FCSTD DOCUMENT  (FreeCAD 0.20R29603 (Git))
Label: cockpit
License: All rights reserved
LicenseURL: http://en.wikipedia.org/wiki/All_rights_reserved
objects: Part::FeaturePython×22, Part::Cylinder×14, Part::Cut×11, Part::MultiFuse×9, Part::Fillet×8, Part::Box×6, Sketcher::SketchObject×4, PartDesign::Pad×4, PartDesign::Body×4, Part::Chamfer×4, Part::Feature×3, Part::Refine×2, Part::Prism×2, Mesh::Feature×1, App::DocumentObjectGroup×1
note: 97 computed .brp shape members not serialized (recipe doc carries the construction recipe); baked Part::Feature solids carry a one-line shape summary decoded from their .brp

FEATURE [Part::Feature] Part__Feature  label="Motedis_45x45"
  Placement = pos=(3,45,0) rot=(0,0,1;0rad)
  shape: bbox 45 x 45 x 1000 mm, 210 faces (baked)
FEATURE [Part::Feature] Part__Feature001  label="Motedis_45x90"
  Placement = pos=(36.25,1.5,0) rot=(0,0,1;0rad)
  shape: bbox 90 x 45 x 1000 mm, 334 faces (baked)
FEATURE [Part::Refine] Part__Feature002  label="Motedis_45x45_refined"
  Source = -> Part__Feature
FEATURE [Part::Refine] Part__Feature001001  label="Motedis_45x90_refined"
  Source = -> Part__Feature001
FEATURE [Part::FeaturePython] Clone  label="Motedis_45x90_refined001"  # Draft clone (typed FeaturePython)
  AttacherType = Attacher::AttachEngine3D
  Fuse = false
  Objects = -> [Part__Feature001001]
  Placement = pos=(0,545,90) rot=(0,1,0;1.5708rad)
  Scale = (1,1,1.3)
FEATURE [Part::FeaturePython] Clone001  label="Motedis_45x90_refined002"  # Draft clone (typed FeaturePython)
  AttacherType = Attacher::AttachEngine3D
  Fuse = false
  Objects = -> [Part__Feature001001]
  Placement = pos=(0,0,90) rot=(0,1,0;1.5708rad)
  Scale = (1,1,1.3)
FEATURE [Part::FeaturePython] Clone002  label="Motedis_45x90_refined003"  # Draft clone (typed FeaturePython)
  AttacherType = Attacher::AttachEngine3D
  Fuse = false
  Objects = -> [Part__Feature001001]
  Placement = pos=(45,45,90) rot=(0.57735,-0.57735,-0.57735;4.18879rad)
  Scale = (1,1,0.5)
FEATURE [Part::FeaturePython] Clone003  label="Motedis_45x90_refined004"  # Draft clone (typed FeaturePython)
  AttacherType = Attacher::AttachEngine3D
  Fuse = false
  Objects = -> [Part__Feature001001]
  Placement = pos=(400,45,90) rot=(0.57735,-0.57735,-0.57735;4.18879rad)
  Scale = (1,1,0.5)
FEATURE [Part::FeaturePython] Clone004  label="Motedis_45x90_refined005"  # Draft clone (typed FeaturePython)
  AttacherType = Attacher::AttachEngine3D
  Fuse = false
  Objects = -> [Part__Feature001001]
  Placement = pos=(1300,45,90) rot=(0.57735,-0.57735,-0.57735;4.18879rad)
  Scale = (1,1,0.5)
FEATURE [Part::FeaturePython] Clone005  label="Motedis_45x90_refined006"  # Draft clone (typed FeaturePython)
  AttacherType = Attacher::AttachEngine3D
  Fuse = false
  Objects = -> [Part__Feature001001]
  Placement = pos=(650,0,90) rot=(0,1,0;0rad)
  Scale = (1,1,0.65)
FEATURE [Part::FeaturePython] Clone006  label="Motedis_45x90_refined007"  # Draft clone (typed FeaturePython)
  AttacherType = Attacher::AttachEngine3D
  Fuse = false
  Objects = -> [Part__Feature001001]
  Placement = pos=(650,545,90) rot=(0,1,0;0rad)
  Scale = (1,1,0.65)
FEATURE [Part::FeaturePython] Clone007  label="Motedis_45x90_refined008"  # Draft clone (typed FeaturePython)
  AttacherType = Attacher::AttachEngine3D
  Fuse = false
  Objects = -> [Part__Feature001001]
  Placement = pos=(740,45,550) rot=(0,0.707107,0.707107;3.14159rad)
  Scale = (1,1,0.5)
FEATURE [Part::FeaturePython] Clone008  label="Motedis_45x45_refined001"  # Draft clone (typed FeaturePython)
  AttacherType = Attacher::AttachEngine3D
  Fuse = false
  Objects = -> [Part__Feature002]
  Placement = pos=(0,72.5,135) rot=(0,1,0;1.5708rad)
  Scale = (1,1,0.4)
FEATURE [Part::FeaturePython] Clone009  label="Motedis_45x45_refined002"  # Draft clone (typed FeaturePython)
  AttacherType = Attacher::AttachEngine3D
  Fuse = false
  Objects = -> [Part__Feature002]
  Placement = pos=(0,472.5,135) rot=(0,1,0;1.5708rad)
  Scale = (1,1,0.4)
FEATURE [Part::Box] Box  label="Cube"
  AttacherType = Attacher::AttachEngine3D
  Height = 20
  Length = 500
  Placement = pos=(826,45,0) rot=(0,1,0;0rad)
  Width = 500
FEATURE [Mesh::Feature] Recaro_Speed_S  label="Recaro+Speed+S"
FEATURE [Part::Feature] Recaro_Speed_S001
  shape: bbox 39.26 x 48.76 x 59.2 mm, 8554 faces, 0 solids (baked)
FEATURE [Part::FeaturePython] Clone010  label="Recaro_Speed_S002"  # Draft clone (typed FeaturePython)
  AttacherType = Attacher::AttachEngine3D
  Fuse = false
  Objects = -> [Recaro_Speed_S001]
  Placement = pos=(532,580,135) rot=(0,0,1;1.5708rad)
  Scale = (14,14,14)
FEATURE [Sketcher::SketchObject] Sketch
  FullyConstrained = true
  MapMode = 5
  Placement = pos=(0,0,0) rot=(1,0,0;1.5708rad)
  Support = -> [XZ_Plane]
  sketch-geometry (9):
    g0: Circle CenterX=0 CenterY=14 CenterZ=0 NormalX=0 NormalY=0 NormalZ=1 AngleXU=0 Radius=4.2
    g1: ArcOfCircle CenterX=0 CenterY=14 CenterZ=0 NormalX=0 NormalY=0 NormalZ=1 AngleXU=0 Radius=9 StartAngle=0.9488 EndAngle=2.19279
    g2: LineSegment StartX=-5.24393 StartY=21.3145 StartZ=0 EndX=-28 EndY=5 EndZ=0
    g3: LineSegment StartX=-28 StartY=5 StartZ=0 EndX=-28 EndY=0 EndZ=0
    g4: LineSegment StartX=-28 StartY=0 StartZ=0 EndX=28 EndY=0 EndZ=0
    g5: LineSegment StartX=28 StartY=0 StartZ=0 EndX=28 EndY=5 EndZ=0
    g6: LineSegment StartX=28 StartY=5 StartZ=0 EndX=5.24393 EndY=21.3145 EndZ=0
    g7: LineSegment StartX=-28 StartY=5 StartZ=0 EndX=28 EndY=5 EndZ=0
    g8: ArcOfCircle CenterX=0 CenterY=14 CenterZ=0 NormalX=0 NormalY=0 NormalZ=1 AngleXU=0 Radius=9 StartAngle=2.19279 EndAngle=7.23199
  constraints (25):
    c: PointOnObject(g0,g-2)
    c: Coincident(g1,g0)
    c: Tangent(g1,g2) = -1.5708
    c: Coincident(g2,g3)
    c: PointOnObject(g3,g-1)
    c: Vertical(g3)
    c: Coincident(g3,g4)
    c: Horizontal(g4)
    c: Coincident(g4,g5)
    c: Vertical(g5)
    c: Coincident(g5,g6)
    c: Tangent(g6,g1) = -1.5708
    c: Radius(g1) = 9
    c: Radius(g0) = 4.2
    c: Equal(g3,g5)
    c: Distance(g3) = 5
    c: Distance(g4) = 56
    c: Equal(g2,g6)
    c: Coincident(g7,g2)
    c: Coincident(g7,g5)
    c: Coincident(g8,g0)
    c: Coincident(g8,g1)
    c: Coincident(g8,g1)
    c: Distance(g0,g-1) = 14
    c: Tangent(g8,g7)
FEATURE [PartDesign::Pad] Pad
  Direction = (0,-1,2e-16)
  Length = 42
  Length2 = 10
  Placement = pos=(0,0,0) rot=(1,0,0;1.5708rad)
  Profile = -> Sketch
  ReferenceAxis = -> Sketch [N_Axis]
  Refine = true
  Type = 0
FEATURE [PartDesign::Body] Body
  Group = -> [Sketch,Pad]
  Origin = -> Origin
  Tip = -> Pad
FEATURE [Part::Box] Box002  label="Cube002"
  AttacherType = Attacher::AttachEngine3D
  Height = 50
  Length = 60
  Placement = pos=(-30,-32,5) rot=(0,0,1;0rad)
  Width = 50
FEATURE [Part::Chamfer] Chamfer
  Base = -> Box002
  Edges = 1 edges r=12: [Edge9]
FEATURE [Part::Cut] Cut
  Base = -> Body
  Refine = true
  Tool = -> Chamfer
FEATURE [Part::Cylinder] Cylinder
  Angle = 360
  AttacherType = Attacher::AttachEngine3D
  FirstAngle = 0
  Height = 12
  Placement = pos=(0,-32,14) rot=(-1,0,0;1.5708rad)
  Radius = 9
  SecondAngle = 0
FEATURE [Part::Cut] Cut001
  Base = -> Cut
  Refine = true
  Tool = -> Cylinder
FEATURE [Part::Cylinder] Cylinder001
  Angle = 360
  AttacherType = Attacher::AttachEngine3D
  FirstAngle = 0
  Height = 10
  Placement = pos=(-16,-12,-1) rot=(0,0,1;0rad)
  Radius = 2.5
  SecondAngle = 0
FEATURE [Part::Cylinder] Cylinder002
  Angle = 360
  AttacherType = Attacher::AttachEngine3D
  FirstAngle = 0
  Height = 10
  Placement = pos=(16,-12,-1) rot=(0,0,1;0rad)
  Radius = 2.5
  SecondAngle = 0
FEATURE [Part::MultiFuse] Fusion
  Refine = true
  Shapes = -> [Cylinder001,Cylinder002]
FEATURE [Part::Cut] Cut002
  Base = -> Cut001
  Refine = true
  Tool = -> Fusion
FEATURE [Part::Fillet] Fillet
  Base = -> Cut002
  Edges = 2 edges r=10: [Edge32,Edge38]
FEATURE [App::DocumentObjectGroup] Group  label="profiles"
  Group = -> [Part__Feature,Part__Feature001,Part__Feature002,Part__Feature001001,Fillet]
FEATURE [Part::Cylinder] Cylinder003
  Angle = 360
  AttacherType = Attacher::AttachEngine3D
  FirstAngle = 0
  Height = 170
  Placement = pos=(0,0,3) rot=(0,0,1;1.5708rad)
  Radius = 39
  SecondAngle = 0
FEATURE [Part::Cylinder] Cylinder004
  Angle = 360
  AttacherType = Attacher::AttachEngine3D
  FirstAngle = 0
  Height = 90
  Placement = pos=(0,0,0) rot=(0,0,1;1.5708rad)
  Radius = 43
  SecondAngle = 0
FEATURE [Part::Cut] Cut003
  Base = -> Cylinder004
  Refine = true
  Tool = -> Cylinder003
FEATURE [Part::Chamfer] Chamfer001
  Base = -> Cut003
  Edges = 2 edges: [Edge2 r=5,Edge5 r=2]
FEATURE [Sketcher::SketchObject] Sketch001
  FullyConstrained = false
  MapMode = 5
  Placement = pos=(0,0,0) rot=(0.57735,0.57735,0.57735;2.0944rad)
  Support = -> [YZ_Plane001]
  sketch-geometry (6):
    g0: LineSegment StartX=-79.5476 StartY=71 StartZ=0 EndX=-12.6037 EndY=71 EndZ=0
    g1: LineSegment StartX=-12.6037 StartY=71 StartZ=0 EndX=-3.6e-15 EndY=89 EndZ=0
    g2: LineSegment StartX=0 StartY=89 StartZ=0 EndX=72.7306 EndY=89 EndZ=0
    g3: LineSegment StartX=72.7306 StartY=89 StartZ=0 EndX=72.7306 EndY=169.697 EndZ=0
    g4: LineSegment StartX=72.7306 StartY=169.697 StartZ=0 EndX=-79.5476 EndY=169.697 EndZ=0
    g5: LineSegment StartX=-79.5476 StartY=169.697 StartZ=0 EndX=-79.5476 EndY=71 EndZ=0
  constraints (15):
    c: Horizontal(g0)
    c: Coincident(g0,g1)
    c: PointOnObject(g1,g-2)
    c: Coincident(g1,g2)
    c: Horizontal(g2)
    c: Coincident(g2,g3)
    c: Vertical(g3)
    c: Coincident(g3,g4)
    c: Horizontal(g4)
    c: Coincident(g4,g5)
    c: Coincident(g5,g0)
    c: Vertical(g5)
    c: Angle(g1,g2) = 2.18166
    c: DistanceY(g0,g1) = 18
    c: DistanceY(g-1,g2) = 89
FEATURE [PartDesign::Pad] Pad001
  Direction = (1,-2e-16,3e-16)
  Length = 100
  Length2 = 10
  Placement = pos=(0,0,0) rot=(0.57735,0.57735,0.57735;2.0944rad)
  Profile = -> Sketch001
  ReferenceAxis = -> Sketch001 [N_Axis]
  Refine = true
  Type = 0
FEATURE [PartDesign::Body] Body001
  Group = -> [Sketch001,Pad001]
  Origin = -> Origin001
  Placement = pos=(-50,0,0) rot=(0,0,1;0rad)
  Tip = -> Pad001
FEATURE [Part::Cut] Cut004
  Base = -> Chamfer001
  Refine = true
  Tool = -> Body001
FEATURE [Part::Cylinder] Cylinder005
  Angle = 360
  AttacherType = Attacher::AttachEngine3D
  FirstAngle = 0
  Height = 170
  Placement = pos=(0,0,-5) rot=(0,0,1;0rad)
  Radius = 22
  SecondAngle = 0
FEATURE [Part::Cut] Cut005
  Base = -> Cut004
  Refine = true
  Tool = -> Cylinder005
FEATURE [Part::Fillet] Fillet001
  Base = -> Cut005
  Edges = 14 edges r=1: [Edge1,Edge3,Edge4,Edge5,Edge6,Edge7,Edge10,Edge11,Edge13,Edge14,Edge15,Edge16,Edge17,Edge18]
FEATURE [Part::Box] Box003  label="Cube003"
  AttacherType = Attacher::AttachEngine3D
  Height = 78.5
  Length = 18
  Placement = pos=(-9,40,5.5) rot=(0,0,1;0rad)
  Width = 16
FEATURE [Part::Cylinder] Cylinder006
  Angle = 360
  AttacherType = Attacher::AttachEngine3D
  FirstAngle = 0
  Height = 11
  Placement = pos=(0,35,76) rot=(-1,0,0;1.5708rad)
  Radius = 7
  SecondAngle = 0
FEATURE [Part::Cylinder] Cylinder007
  Angle = 360
  AttacherType = Attacher::AttachEngine3D
  FirstAngle = 0
  Height = 30
  Placement = pos=(0,35,76) rot=(-1,0,0;1.5708rad)
  Radius = 4.2
  SecondAngle = 0
FEATURE [Part::Box] Box004  label="Cube004"
  AttacherType = Attacher::AttachEngine3D
  Height = 78.5
  Length = 10
  Placement = pos=(-5,44,5.5) rot=(0,0,1;0rad)
  Width = 14.3
FEATURE [Part::MultiFuse] Fusion001
  Refine = true
  Shapes = -> [Fillet001,Box003,Box004]
FEATURE [Part::MultiFuse] Fusion002
  Refine = true
  Shapes = -> [Cylinder007,Cylinder006]
FEATURE [Part::Cylinder] Cylinder008
  Angle = 360
  AttacherType = Attacher::AttachEngine3D
  FirstAngle = 0
  Height = 11
  Placement = pos=(0,35,76) rot=(-1,0,0;1.5708rad)
  Radius = 7
  SecondAngle = 0
FEATURE [Part::Cylinder] Cylinder009
  Angle = 360
  AttacherType = Attacher::AttachEngine3D
  FirstAngle = 0
  Height = 30
  Placement = pos=(0,35,76) rot=(-1,0,0;1.5708rad)
  Radius = 4.2
  SecondAngle = 0
FEATURE [Part::MultiFuse] Fusion003
  Placement = pos=(0,0,-50) rot=(0,0,1;0rad)
  Refine = true
  Shapes = -> [Cylinder009,Cylinder008]
FEATURE [Part::MultiFuse] Fusion004
  Refine = true
  Shapes = -> [Fusion002,Fusion003]
FEATURE [Part::Cut] Cut006
  Base = -> Fusion001
  Refine = true
  Tool = -> Fusion004
FEATURE [Part::Fillet] Fillet002
  Base = -> Cut006
  Edges = 2 edges r=4: [Edge14,Edge24]
FEATURE [Part::Fillet] Fillet003
  Base = -> Fillet002
  Edges = 2 edges r=1: [Edge116,Edge120]
FEATURE [Part::FeaturePython] Clone015  label="Motedis_45x45_refined003"  # Draft clone (typed FeaturePython)
  AttacherType = Attacher::AttachEngine3D
  Fuse = false
  Objects = -> [Part__Feature002]
  Placement = pos=(1184.3,0,90) rot=(0,0,1;0rad)
  Scale = (1,1,0.11)
FEATURE [Part::FeaturePython] Clone016  label="Motedis_45x45_refined004"  # Draft clone (typed FeaturePython)
  AttacherType = Attacher::AttachEngine3D
  Fuse = false
  Objects = -> [Part__Feature002]
  Placement = pos=(1184.3,545,90) rot=(0,0,1;0rad)
  Scale = (1,1,0.11)
FEATURE [Part::FeaturePython] Clone017  label="Fillet004"  # Draft clone (typed FeaturePython)
  AttacherType = Attacher::AttachEngine3D
  Fuse = false
  Objects = -> [Fillet]
  Placement = pos=(0,503,0) rot=(1,0,0;3.14159rad)
  Scale = (1,1,1)
FEATURE [Part::FeaturePython] Clone018  label="Fillet005"  # Draft clone (typed FeaturePython)
  AttacherType = Attacher::AttachEngine3D
  Fuse = false
  Objects = -> [Fillet]
  Placement = pos=(284,503,0) rot=(1,0,0;3.14159rad)
  Scale = (1,1,1)
FEATURE [Part::FeaturePython] Clone019  label="Fillet006"  # Draft clone (typed FeaturePython)
  AttacherType = Attacher::AttachEngine3D
  Fuse = false
  Objects = -> [Fillet]
  Placement = pos=(0,87,0) rot=(0,1,0;3.14159rad)
  Scale = (1,1,1)
FEATURE [Part::FeaturePython] Clone020  label="Fillet007"  # Draft clone (typed FeaturePython)
  AttacherType = Attacher::AttachEngine3D
  Fuse = false
  Objects = -> [Fillet]
  Placement = pos=(284,87,0) rot=(0,1,0;3.14159rad)
  Scale = (1,1,1)
FEATURE [Part::MultiFuse] Fusion005
  Placement = pos=(934,0,0) rot=(0,1,0;0rad)
  Refine = true
  Shapes = -> [Clone017,Clone018,Clone019,Clone020]
FEATURE [Part::FeaturePython] Clone021  label="Motedis_45x90_refined009"  # Draft clone (typed FeaturePython)
  AttacherType = Attacher::AttachEngine3D
  Fuse = false
  Objects = -> [Part__Feature001001]
  Placement = pos=(83,93,0) rot=(0,-1,0;1.5708rad)
  Scale = (1,1,1)
FEATURE [Sketcher::SketchObject] Sketch002
  FullyConstrained = true
  MapMode = 5
  Placement = pos=(0,0,0) rot=(1,0,0;1.5708rad)
  Support = -> [XZ_Plane002]
  sketch-geometry (29):
    g0: LineSegment StartX=-23 StartY=75 StartZ=0 EndX=23 EndY=75 EndZ=0
    g1: LineSegment StartX=23 StartY=75 StartZ=0 EndX=23 EndY=5 EndZ=0
    g2: LineSegment StartX=23 StartY=5 StartZ=0 EndX=-23 EndY=5 EndZ=0
    g3: LineSegment StartX=-23 StartY=5 StartZ=0 EndX=-23 EndY=75 EndZ=0
    g4: Circle CenterX=-13.5 CenterY=67.5 CenterZ=0 NormalX=0 NormalY=0 NormalZ=1 AngleXU=0 Radius=4.2
    g5: Circle CenterX=-13.5 CenterY=12.5 CenterZ=0 NormalX=0 NormalY=0 NormalZ=1 AngleXU=0 Radius=4.2
    g6: Circle CenterX=13.5 CenterY=12.5 CenterZ=0 NormalX=0 NormalY=0 NormalZ=1 AngleXU=0 Radius=4.2
    g7: Circle CenterX=13.5 CenterY=67.5 CenterZ=0 NormalX=0 NormalY=0 NormalZ=1 AngleXU=0 Radius=4.2
    g8: LineSegment StartX=-13.5 StartY=67.5 StartZ=0 EndX=13.5 EndY=67.5 EndZ=0
    g9: LineSegment StartX=13.5 StartY=67.5 StartZ=0 EndX=13.5 EndY=12.5 EndZ=0
    g10: LineSegment StartX=13.5 StartY=12.5 StartZ=0 EndX=-13.5 EndY=12.5 EndZ=0
    g11: LineSegment StartX=-13.5 StartY=12.5 StartZ=0 EndX=-13.5 EndY=67.5 EndZ=0
    g12: LineSegment StartX=-23 StartY=75 StartZ=0 EndX=-13.5 EndY=67.5 EndZ=0
    g13: LineSegment StartX=-13.5 StartY=12.5 StartZ=0 EndX=-23 EndY=5 EndZ=0
    g14: LineSegment StartX=13.5 StartY=12.5 StartZ=0 EndX=23 EndY=5 EndZ=0
    g15: LineSegment StartX=13.5 StartY=67.5 StartZ=0 EndX=23 EndY=75 EndZ=0
    g16: LineSegment StartX=-27 StartY=0 StartZ=0 EndX=27 EndY=0 EndZ=0
    g17: LineSegment StartX=27 StartY=0 StartZ=0 EndX=42.2818 EndY=11.2123 EndZ=0
    g18: LineSegment StartX=47.0765 StartY=27.5006 StartZ=0 EndX=27 EndY=80 EndZ=0
    g19: LineSegment StartX=27 StartY=80 StartZ=0 EndX=-27 EndY=80 EndZ=0
    g20: LineSegment StartX=-27 StartY=80 StartZ=0 EndX=-47.0765 EndY=27.5006 EndZ=0
    g21: LineSegment StartX=-42.2818 StartY=11.2123 StartZ=0 EndX=-27 EndY=0 EndZ=0
    g22: Circle CenterX=-34 CenterY=22.5 CenterZ=0 NormalX=0 NormalY=0 NormalZ=1 AngleXU=0 Radius=4.2
    g23: Circle CenterX=34 CenterY=22.5 CenterZ=0 NormalX=0 NormalY=0 NormalZ=1 AngleXU=0 Radius=4.2
    g24: ArcOfCircle CenterX=-34 CenterY=22.5 CenterZ=0 NormalX=0 NormalY=0 NormalZ=1 AngleXU=0 Radius=14 StartAngle=2.77634 EndAngle=4.0794
    g25: ArcOfCircle CenterX=34 CenterY=22.5 CenterZ=0 NormalX=0 NormalY=0 NormalZ=1 AngleXU=0 Radius=14 StartAngle=5.34538 EndAngle=6.64844
    g26: LineSegment StartX=-27 StartY=80 StartZ=0 EndX=-27 EndY=0 EndZ=0
    g27: LineSegment StartX=-34 StartY=22.5 StartZ=0 EndX=0 EndY=22.5 EndZ=0
    g28: LineSegment StartX=0 StartY=22.5 StartZ=0 EndX=34 EndY=22.5 EndZ=0
  constraints (70):
    c: Coincident(g0,g1)
    c: Coincident(g1,g2)
    c: Coincident(g2,g3)
    c: Coincident(g3,g0)
    c: Horizontal(g0)
    c: Vertical(g1)
    c: Vertical(g3)
    c: Distance(g1) = 70
    c: Distance(g0) = 46
    c: Coincident(g8,g9)
    c: Coincident(g9,g10)
    c: Coincident(g10,g11)
    c: Coincident(g11,g8)
    c: Horizontal(g8)
    c: Horizontal(g10)
    c: Vertical(g9)
    c: Vertical(g11)
    c: Coincident(g6,g9)
    c: Coincident(g5,g10)
    c: Coincident(g8,g4)
    c: Coincident(g7,g8)
    c: Distance(g8) = 27
    c: Distance(g11) = 55
    c: Equal(g5,g4)
    c: Equal(g5,g7)
    c: Equal(g5,g6)
    c: Radius(g5) = 4.2
    c: Coincident(g12,g0)
    c: Coincident(g12,g4)
    c: Coincident(g13,g5)
    c: Coincident(g13,g2)
    c: Coincident(g14,g6)
    c: Coincident(g14,g1)
    c: Coincident(g15,g7)
    c: Coincident(g15,g0)
    c: Equal(g14,g13)
    c: Equal(g13,g12)
    c: DistanceY(g-1,g7) = 67.5
    c: Symmetric(g1,g2,g-2)
    c: Coincident(g16,g17)
    c: Coincident(g18,g19)
    c: Coincident(g19,g20)
    c: Coincident(g21,g16)
    c: Equal(g20,g18)
    c: Symmetric(g16,g16,g-2)
    c: Symmetric(g19,g18,g-2)
    c: Equal(g22,g23)
    c: Equal(g23,g5)
    c: Coincident(g24,g22)
    c: Coincident(g25,g23)
    c: Tangent(g25,g18) = -1.5708
    c: Tangent(g25,g17) = -1.5708
    c: DistanceY(g-1,g22) = 22.5
    c: DistanceX(g-1,g23) = 34
    c: Radius(g25) = 14
    c: Equal(g25,g24)
    c: PointOnObject(g16,g-1)
    c: Distance(g16) = 54
    c: Coincident(g26,g19)
    c: Coincident(g26,g16)
    c: Vertical(g26)
    c: Tangent(g24,g20) = -1.5708
    c: DistanceY(g0,g19) = 5
    c: Coincident(g27,g22)
    c: PointOnObject(g27,g-2)
    c: Horizontal(g27)
    c: Coincident(g28,g27)
    c: Coincident(g28,g23)
    c: Horizontal(g28)
    c: Tangent(g24,g21) = -1.5708
FEATURE [PartDesign::Pad] Pad002
  Direction = (0,-1,2e-16)
  Length = 10
  Length2 = 10
  Placement = pos=(0,0,0) rot=(1,0,0;1.5708rad)
  Profile = -> Sketch002
  ReferenceAxis = -> Sketch002 [N_Axis]
  Refine = true
  Type = 0
FEATURE [PartDesign::Body] Body002
  Group = -> [Sketch002,Pad002]
  Origin = -> Origin002
  Tip = -> Pad002
FEATURE [Part::Prism] Prism
  AttacherType = Attacher::AttachEngine3D
  Circumradius = 7.6
  FirstAngle = 0
  Height = 20
  Placement = pos=(13.5,-4,13.5) rot=(1,0,0;1.5708rad)
  Polygon = 6
  SecondAngle = 0
FEATURE [Part::Prism] Prism001
  AttacherType = Attacher::AttachEngine3D
  Circumradius = 7.6
  FirstAngle = 0
  Height = 20
  Placement = pos=(-13.5,-4,13.5) rot=(1,0,0;1.5708rad)
  Polygon = 6
  SecondAngle = 0
FEATURE [Part::MultiFuse] Fusion006
  Refine = true
  Shapes = -> [Prism001,Prism]
FEATURE [Part::Cut] Cut007
  Base = -> Pad002
  Refine = true
  Tool = -> Fusion006
FEATURE [Part::Fillet] Fillet004  label="Fillet008"
  Base = -> Cut007
  Edges = 4 edges r=5: [Edge1,Edge2,Edge45,Edge46]
FEATURE [Part::Fillet] Fillet005  label="Fillet009"
  Base = -> Fillet004
  Edges = 1 edges r=2: [Edge11]
FEATURE [Part::FeaturePython] Clone022  label="Fillet010"  # Draft clone (typed FeaturePython)
  AttacherType = Attacher::AttachEngine3D
  Fuse = false
  Objects = -> [Fillet005]
  Placement = pos=(-10,109,0) rot=(0,0,1;1.5708rad)
  Scale = (1,1,1)
FEATURE [Part::FeaturePython] Clone023  label="Fillet011"  # Draft clone (typed FeaturePython)
  AttacherType = Attacher::AttachEngine3D
  Fuse = false
  Objects = -> [Fillet005]
  Placement = pos=(-10,481,0) rot=(0,0,1;1.5708rad)
  Scale = (1,1,1)
FEATURE [Part::Box] Box005  label="Cube005"
  AttacherType = Attacher::AttachEngine3D
  Height = 20
  Length = 90
  Width = 40
FEATURE [Part::Chamfer] Chamfer002
  Base = -> Box005
  Edges = 2 edges r=14: [Edge4,Edge8]
FEATURE [Part::Box] Box006  label="Cube006"
  AttacherType = Attacher::AttachEngine3D
  Height = 5.3
  Length = 90
  Placement = pos=(0,15,17) rot=(0,0,1;0rad)
  Width = 10
FEATURE [Part::MultiFuse] Fusion007
  Refine = true
  Shapes = -> [Box006,Chamfer002]
FEATURE [Part::Fillet] Fillet006  label="Fillet012"
  Base = -> Fusion007
  Edges = 14 edges r=1.2: [Edge1,Edge2,Edge3,Edge5,Edge6,Edge10,Edge11,Edge12,Edge17,Edge18,Edge19,Edge20,Edge29,Edge30]
FEATURE [Part::Chamfer] Chamfer003
  Base = -> Fillet006
  Edges = 2 edges r=0.4: [Edge32,Edge56]
FEATURE [Part::Cylinder] Cylinder010
  Angle = 360
  AttacherType = Attacher::AttachEngine3D
  FirstAngle = 0
  Height = 20
  Placement = pos=(45,20,-10) rot=(0,0,1;0rad)
  Radius = 7
  SecondAngle = 0
FEATURE [Part::Cylinder] Cylinder011
  Angle = 360
  AttacherType = Attacher::AttachEngine3D
  FirstAngle = 0
  Height = 40
  Placement = pos=(45,20,-10) rot=(0,0,1;0rad)
  Radius = 4.2
  SecondAngle = 0
FEATURE [Part::MultiFuse] Fusion008
  Refine = true
  Shapes = -> [Cylinder010,Cylinder011]
FEATURE [Part::Cut] Cut008
  Base = -> Chamfer003
  Refine = true
  Tool = -> Fusion008
FEATURE [Part::Cylinder] Cylinder012
  Angle = 360
  AttacherType = Attacher::AttachEngine3D
  FirstAngle = 0
  Height = 40
  Placement = pos=(22.5,8,-10) rot=(0,0,1;0rad)
  Radius = 4
  SecondAngle = 0
FEATURE [Part::FeaturePython] Array  # Draft array (typed FeaturePython)
  AlwaysSyncPlacement = false
  Angle = 360
  ArrayType = 0
  Axis = (0,0,1)
  Base = -> Cylinder012
  Center = (0,0,0)
  Count = 8
  ExpandArray = false
  Fuse = true
  IntervalAxis = (0,0,0)
  IntervalX = (15,0,0)
  IntervalY = (0,24,0)
  IntervalZ = (0,0,100)
  NumberCircles = 3
  NumberPolar = 5
  NumberX = 4
  NumberY = 2
  NumberZ = 1
  PlacementList = 8 placements: [(22.5,8,-10),(22.5,32,-10),(37.5,8,-10),(37.5,32,-10),(52.5,8,-10),(52.5,32,-10),(67.5,8,-10),(67.5,32,-10)]
  RadialDistance = 50
  ScaleList = (8) [(1,1,1),(1,1,1),(1,1,1),(1,1,1),(1,1,1),(1,1,1),(1,1,1),(1,1,1)]
  Symmetry = 1
  TangentialDistance = 25
FEATURE [Part::Cut] Cut009
  Base = -> Cut008
  Refine = true
  Tool = -> Array
FEATURE [Sketcher::SketchObject] Sketch003
  FullyConstrained = true
  MapMode = 5
  Placement = pos=(0,0,0) rot=(0.57735,0.57735,0.57735;2.0944rad)
  Support = -> [YZ_Plane003]
  sketch-geometry (20):
    g0: LineSegment StartX=17.5 StartY=5.9 StartZ=0 EndX=17.1 EndY=6.3767 EndZ=0
    g1: LineSegment StartX=17.1 StartY=6.3767 StartZ=0 EndX=18 EndY=10 EndZ=0
    g2: LineSegment StartX=18 StartY=10 StartZ=0 EndX=20.5 EndY=10 EndZ=0
    g3: LineSegment StartX=20.5 StartY=10 StartZ=0 EndX=20.5 EndY=1 EndZ=0
    g4: LineSegment StartX=20.5 StartY=1 StartZ=0 EndX=24.5 EndY=1 EndZ=0
    g5: LineSegment StartX=24.5 StartY=1 StartZ=0 EndX=24.5 EndY=10 EndZ=0
    g6: LineSegment StartX=24.5 StartY=10 StartZ=0 EndX=27 EndY=10 EndZ=0
    g7: LineSegment StartX=27 StartY=10 StartZ=0 EndX=27.9 EndY=6.3767 EndZ=0
    g8: LineSegment StartX=27.9 StartY=6.3767 StartZ=0 EndX=27.5 EndY=5.9 EndZ=0
    g9: LineSegment StartX=27.5 StartY=5.9 StartZ=0 EndX=27.5 EndY=0 EndZ=0
    g10: LineSegment StartX=27.5 StartY=0 StartZ=0 EndX=42 EndY=0 EndZ=0
    g11: LineSegment StartX=42 StartY=0 StartZ=0 EndX=42 EndY=-8 EndZ=0
    g12: LineSegment StartX=42 StartY=-8 StartZ=0 EndX=3 EndY=-8 EndZ=0
    g13: LineSegment StartX=3 StartY=-8 StartZ=0 EndX=3 EndY=0 EndZ=0
    g14: LineSegment StartX=3 StartY=0 StartZ=0 EndX=17.5 EndY=0 EndZ=0
    g15: LineSegment StartX=17.5 StartY=0 StartZ=0 EndX=17.5 EndY=5.9 EndZ=0
    g16: LineSegment StartX=17.5 StartY=0 StartZ=0 EndX=27.5 EndY=0 EndZ=0
    g17: LineSegment StartX=20.5 StartY=10 StartZ=0 EndX=24.5 EndY=10 EndZ=0
    g18: LineSegment StartX=17.5 StartY=0 StartZ=0 EndX=20.5 EndY=1 EndZ=0
    g19: LineSegment StartX=24.5 StartY=1 StartZ=0 EndX=27.5 EndY=0 EndZ=0
  constraints (56):
    c: Coincident(g0,g1)
    c: Coincident(g1,g2)
    c: Horizontal(g2)
    c: Coincident(g2,g3)
    c: Vertical(g3)
    c: Coincident(g3,g4)
    c: Horizontal(g4)
    c: Coincident(g4,g5)
    c: Coincident(g5,g6)
    c: Horizontal(g6)
    c: Coincident(g6,g7)
    c: Coincident(g7,g8)
    c: Coincident(g8,g9)
    c: Vertical(g9)
    c: Coincident(g9,g10)
    c: Horizontal(g10)
    c: Coincident(g10,g11)
    c: Vertical(g11)
    c: Coincident(g11,g12)
    c: Horizontal(g12)
    c: Coincident(g12,g13)
    c: Vertical(g13)
    c: Coincident(g13,g14)
    c: Horizontal(g14)
    c: Coincident(g14,g15)
    c: Coincident(g15,g0)
    c: Vertical(g15)
    c: Vertical(g5)
    c: PointOnObject(g13,g-1)
    c: Distance(g12) = 39
    c: Coincident(g16,g14)
    c: Coincident(g16,g9)
    c: Horizontal(g16)
    c: Equal(g2,g6)
    c: Coincident(g17,g2)
    c: Coincident(g17,g5)
    c: Horizontal(g17)
    c: Equal(g1,g7)
    c: Equal(g0,g8)
    c: Equal(g9,g15)
    c: Equal(g14,g10)
    c: Distance(g16) = 10
    c: Distance(g-1,g13) = 3
    c: Coincident(g18,g14)
    c: Coincident(g18,g3)
    c: Coincident(g19,g4)
    c: Coincident(g19,g9)
    c: Equal(g18,g19)
    c: DistanceY(g13,g0) = 5.9
    c: Angle(g0,g15) = 2.44346
    c: DistanceX(g0,g0) = 0.4
    c: DistanceY(g13,g1) = 10
    c: Distance(g2) = 2.5
    c: Distance(g3,g16) = 1
    c: DistanceX(g0,g1) = 0.5
    c: Distance(g13) = 8
FEATURE [PartDesign::Pad] Pad003
  Direction = (1,-2e-16,3e-16)
  Length = 90
  Length2 = 10
  Placement = pos=(0,0,0) rot=(0.57735,0.57735,0.57735;2.0944rad)
  Profile = -> Sketch003
  ReferenceAxis = -> Sketch003 [N_Axis]
  Refine = true
  Type = 0
FEATURE [PartDesign::Body] Body003
  Group = -> [Sketch003,Pad003]
  Origin = -> Origin003
  Tip = -> Pad003
FEATURE [Part::Cylinder] Cylinder013
  Angle = 360
  AttacherType = Attacher::AttachEngine3D
  FirstAngle = 0
  Height = 40
  Placement = pos=(9,10,-10) rot=(0,0,1;0rad)
  Radius = 2
  SecondAngle = 0
FEATURE [Part::FeaturePython] Array001  # Draft array (typed FeaturePython)
  AlwaysSyncPlacement = false
  Angle = 360
  ArrayType = 0
  Axis = (0,0,1)
  Base = -> Cylinder013
  Center = (0,0,0)
  Count = 10
  ExpandArray = false
  Fuse = true
  IntervalAxis = (0,0,0)
  IntervalX = (18,0,0)
  IntervalY = (0,25,0)
  IntervalZ = (0,0,100)
  NumberCircles = 3
  NumberPolar = 5
  NumberX = 5
  NumberY = 2
  NumberZ = 1
  PlacementList = 10 placements: [(9,10,-10),(9,35,-10),(27,10,-10),(27,35,-10),(45,10,-10),(45,35,-10),(63,10,-10),(63,35,-10),(81,10,-10),(81,35,-10)]
  RadialDistance = 50
  ScaleList = (10) [(1,1,1),(1,1,1),(1,1,1),(1,1,1),(1,1,1),(1,1,1),(1,1,1),(1,1,1),(1,1,1),(1,1,1)]
  Symmetry = 1
  TangentialDistance = 25
FEATURE [Part::Cut] Cut010
  Base = -> Body003
  Refine = true
  Tool = -> Array001
FEATURE [Part::Fillet] Fillet007  label="Fillet013"
  Base = -> Cut010
  Edges = 8 edges r=3: [Edge20,Edge21,Edge22,Edge33,Edge34,Edge35,Edge57,Edge58]
